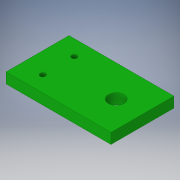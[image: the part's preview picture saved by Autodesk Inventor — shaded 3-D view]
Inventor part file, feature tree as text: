
AUTODESK INVENTOR PART (.ipt)
format: ipt  version: 2017 SP1 (Build 210196100, 196)  size: 104,960 bytes
history: native  units: in
note: dims shown in document units (in); Inventor stores cm internally (conversion verified against a paired STEP export)
features: extrude x1, sketch x1
ambient origin geometry x8: Origin, YZ Plane, XZ Plane, XY Plane, X Axis, Y Axis, Z Axis, Center Point
bodies: Solid1 (feature_tree)
feature tree (2):
  extrude  "Extrusion1"  Depth=1.5in
  sketch  "Sketch1"  dims[d0=2.5in d1=1.5in d2=1.0in d3=0.375in d4=0.875in d5=0.25in d6=0.0in d7=0.5in d8=0.125in]
